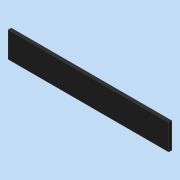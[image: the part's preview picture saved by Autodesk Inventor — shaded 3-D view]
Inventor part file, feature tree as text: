
AUTODESK INVENTOR PART (.ipt)
format: ipt  version: 2020 (Build 240168000, 168)  size: 87,552 bytes
history: native  units: mm
features: other x1, extrude x1
ambient origin geometry x8: Origin, YZ Plane, XZ Plane, XY Plane, X Axis, Y Axis, Z Axis, Center Point
bodies: Body1 (feature_tree)
feature tree (2):
  other  "實體1"
  extrude  "擠出1"  Depth=20.0mm
